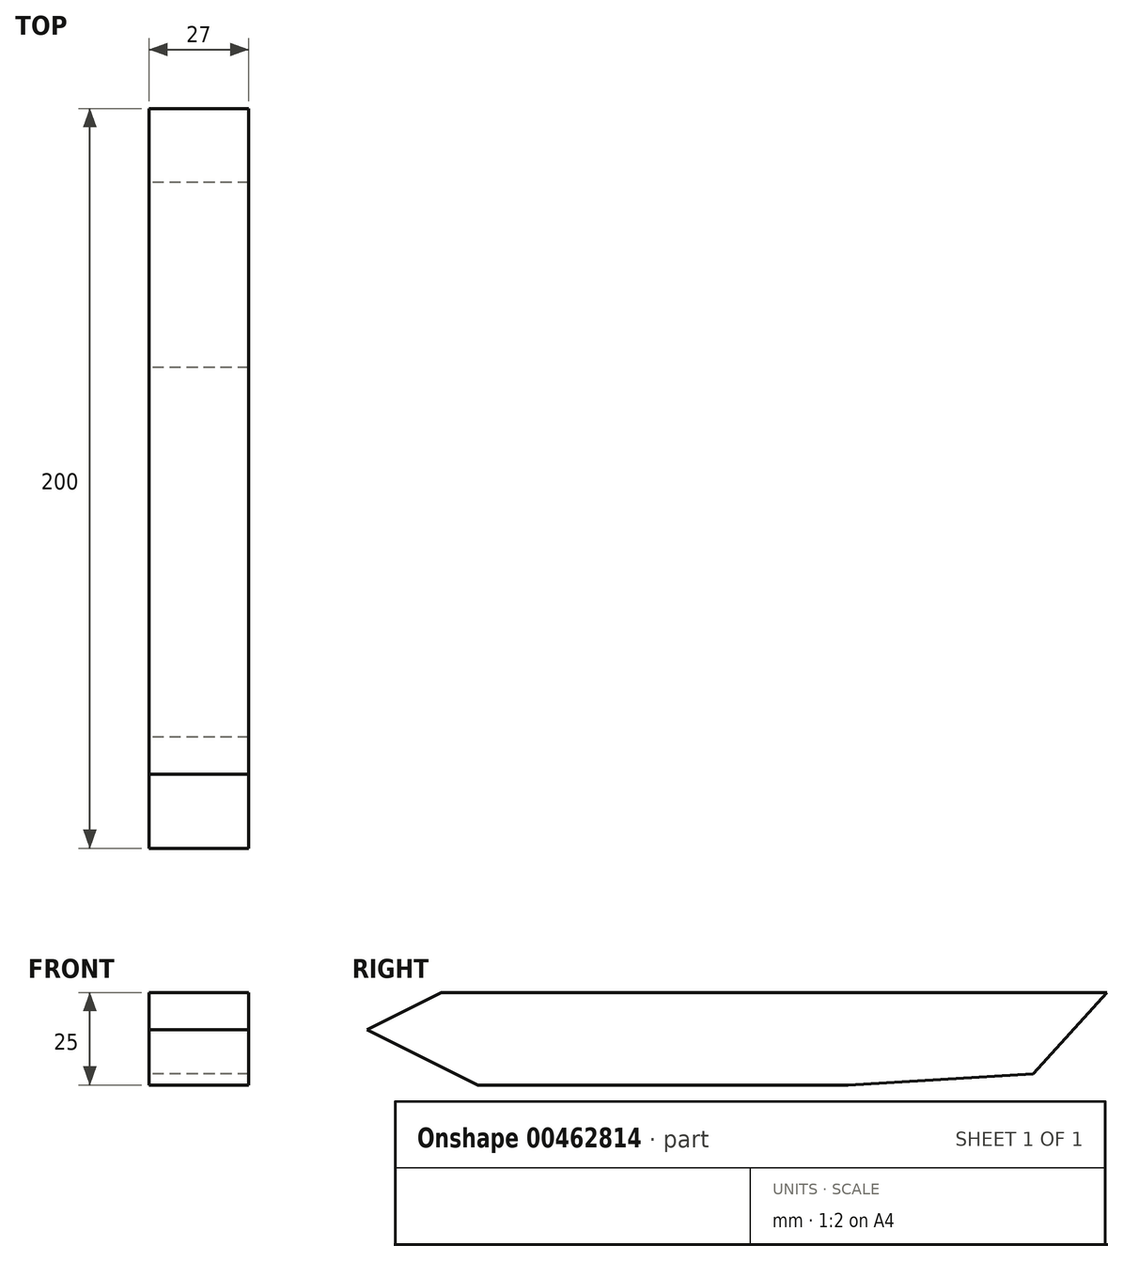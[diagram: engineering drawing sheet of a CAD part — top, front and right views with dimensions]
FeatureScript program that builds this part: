
annotation { "Feature Type Name" : "Feature", "Feature Type Description" : "" }
export const myFeature = defineFeature(function(context is Context, id is Id, definition is map)
    precondition{}
    {
        {
            var Q0;
            Q0=qCreatedBy(makeId("Right.planeOp"),FACE);
            var sketch = newSketch(context, id + "F0", { "sketchPlane" : qUnion([Q0])});
            skLineSegment(sketch, "E0", {"start": v(-98.02, 34.23) * mm, "end": v(81.98, 34.23) * mm});
            skLineSegment(sketch, "E1", {"start": v(81.98, 34.23) * mm, "end": v(61.98, 12.23) * mm});
            skLineSegment(sketch, "E2", {"start": v(61.98, 12.23) * mm, "end": v(11.98, 9.23) * mm});
            skLineSegment(sketch, "E3", {"start": v(11.98, 9.23) * mm, "end": v(-88.02, 9.23) * mm});
            skLineSegment(sketch, "E4", {"start": v(-88.02, 9.23) * mm, "end": v(-118.02, 24.23) * mm});
            skLineSegment(sketch, "E5", {"start": v(-118.02, 24.23) * mm, "end": v(-98.02, 34.23) * mm});
            skSolve(sketch);
        }
        {
            var Q0;
            Q0=makeQuery(id+"F0.imprint","IMPRINT",FACE,{"disambiguationData":[TD([[makeQuery(id+"F0.imprint","IMPRINT",EDGE,{"derivedFrom":sQuery(id+"F0.wireOp",EDGE,"E0")}),-1.0]])]});
            extrude(context, id + "F1", {"entities" : qUnion([Q0]), "depth" : 27 * mm});
        }
        {
            var Q0;
            Q0=makeQuery(id+"F1.opExtrude","SWEPT_FACE",FACE,{"disambiguationData":[OSD([sQuery(id+"F0.wireOp",EDGE,"E0")])]});
            var sketch = newSketch(context, id + "F2", { "sketchPlane" : qUnion([Q0])});
            skFitSpline(sketch, "E6", {"points": [v(3.97, 81.98) * mm, v(22.8, 29.46) * mm, v(20.83, -98.02) * mm], "startDerivative": vector(57.4, -116) * mm, "endDerivative": vector(-18.53, -235.86) * mm});
            skSolve(sketch);
        }
        {
            var Q0;
            {var subQ0=sQuery(id+"F2.wireOp",EDGE,"E6");Q0=makeQuery(id+"F2.imprint","IMPRINT",FACE,{"disambiguationData":[TD([[makeQuery(id+"F2.imprint","IMPRINT",EDGE,{"derivedFrom":subQ0}),1.0]])]});}
            var Q1;
            Q1=sQuery(id+"F2.wireOp",EDGE,"E6");
            extrude(context, id + "F3", {"entities" : qUnion([Q0]), "bodyType" : ToolBodyType.SURFACE, "operationType" : NewBodyOperationType.REMOVE, "surfaceEntities" : qUnion([Q1]), "oppositeDirection" : true, "depth" : 25 * mm, "hasSecondDirection" : true, "secondDirectionOppositeDirection" : false, "secondDirectionDepth" : 25 * mm});
        }
    });
